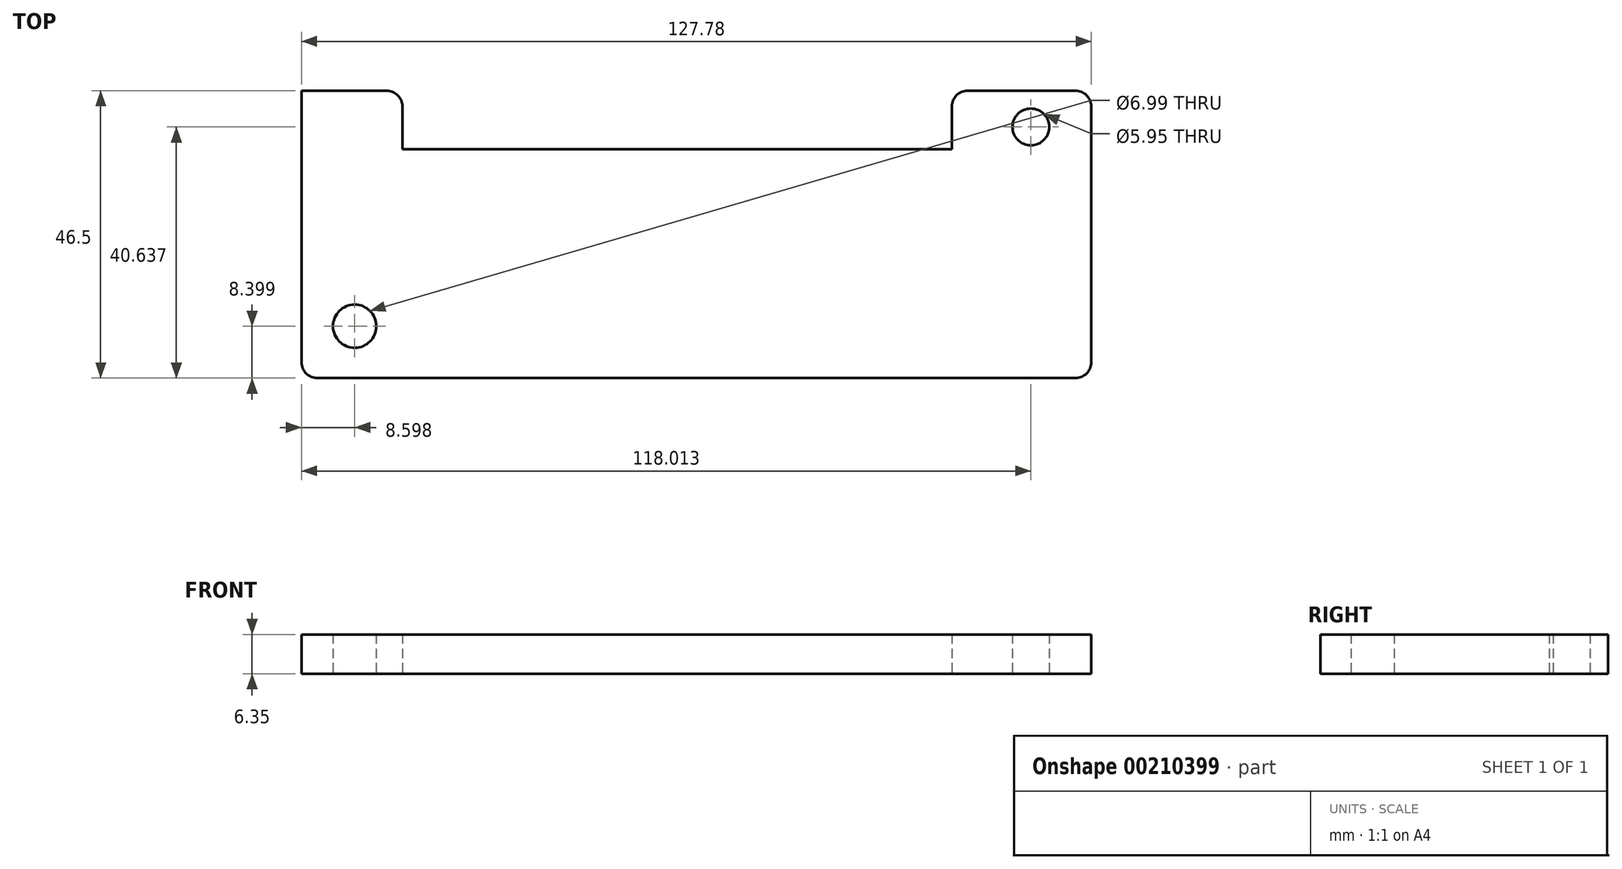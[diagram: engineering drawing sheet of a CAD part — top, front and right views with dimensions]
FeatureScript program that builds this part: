
annotation { "Feature Type Name" : "Feature", "Feature Type Description" : "" }
export const myFeature = defineFeature(function(context is Context, id is Id, definition is map)
    precondition{}
    {
        {
            var Q0;
            Q0=qCreatedBy(makeId("Top.planeOp"),FACE);
            var sketch = newSketch(context, id + "F0", { "sketchPlane" : qUnion([Q0])});
            skLineSegment(sketch, "E0.bottom", {"start": v(-63.1, 20.8) * mm, "end": v(-49.33, 20.8) * mm});
            skLineSegment(sketch, "E0.top", {"start": v(-60.57, -25.7) * mm, "end": v(62.13, -25.7) * mm});
            skLineSegment(sketch, "E0.left", {"start": v(-63.1, 20.8) * mm, "end": v(-63.1, -23.15) * mm});
            skLineSegment(sketch, "E0.right", {"start": v(64.67, 18.27) * mm, "end": v(64.67, -23.15) * mm});
            skCircle(sketch, "E1", {"center": v(-54.51, -17.3) * mm, "radius": 3.5 * mm});
            skCircle(sketch, "E2", {"center": v(54.9, 14.95) * mm, "radius": 2.98 * mm});
            skLineSegment(sketch, "E3.top", {"start": v(-46.8, 11.33) * mm, "end": v(42.1, 11.33) * mm});
            skLineSegment(sketch, "E3.left", {"start": v(-46.8, 18.27) * mm, "end": v(-46.8, 11.33) * mm});
            skLineSegment(sketch, "E3.right", {"start": v(42.1, 18.27) * mm, "end": v(42.1, 11.33) * mm});
            skLineSegment(sketch, "E4.trimOffspring", {"start": v(44.65, 20.8) * mm, "end": v(62.13, 20.8) * mm});
            skPoint(sketch, "E5.visualSharp", {"position": v(-46.8, 20.8) * mm});
            skArc(sketch, "E5.filletArc", {"start": v(-46.8, 18.27) * mm, "mid": v(-47.54, 20.06) * mm, "end": v(-49.33, 20.8) * mm});
            skPoint(sketch, "E6.visualSharp", {"position": v(42.1, 20.8) * mm});
            skArc(sketch, "E6.filletArc", {"start": v(44.65, 20.8) * mm, "mid": v(42.85, 20.06) * mm, "end": v(42.1, 18.27) * mm});
            skPoint(sketch, "E7.visualSharp", {"position": v(64.67, 20.8) * mm});
            skArc(sketch, "E7.filletArc", {"start": v(64.67, 18.27) * mm, "mid": v(63.93, 20.06) * mm, "end": v(62.13, 20.8) * mm});
            skPoint(sketch, "E8.visualSharp", {"position": v(64.67, -25.7) * mm});
            skArc(sketch, "E8.filletArc", {"start": v(62.13, -25.7) * mm, "mid": v(63.93, -24.95) * mm, "end": v(64.67, -23.15) * mm});
            skPoint(sketch, "E9.visualSharp", {"position": v(-63.1, -25.7) * mm});
            skArc(sketch, "E9.filletArc", {"start": v(-63.1, -23.15) * mm, "mid": v(-62.37, -24.95) * mm, "end": v(-60.57, -25.7) * mm});
            skSolve(sketch);
        }
        {
            var Q0;
            Q0=makeQuery(id+"F0.imprint","IMPRINT",FACE,{"disambiguationData":[TD([[makeQuery(id+"F0.imprint","IMPRINT",EDGE,{"derivedFrom":sQuery(id+"F0.wireOp",EDGE,"E0.bottom")}),-1.0]])]});
            extrude(context, id + "F1", {"entities" : qUnion([Q0]), "depth" : 6.35 * mm});
        }
    });
